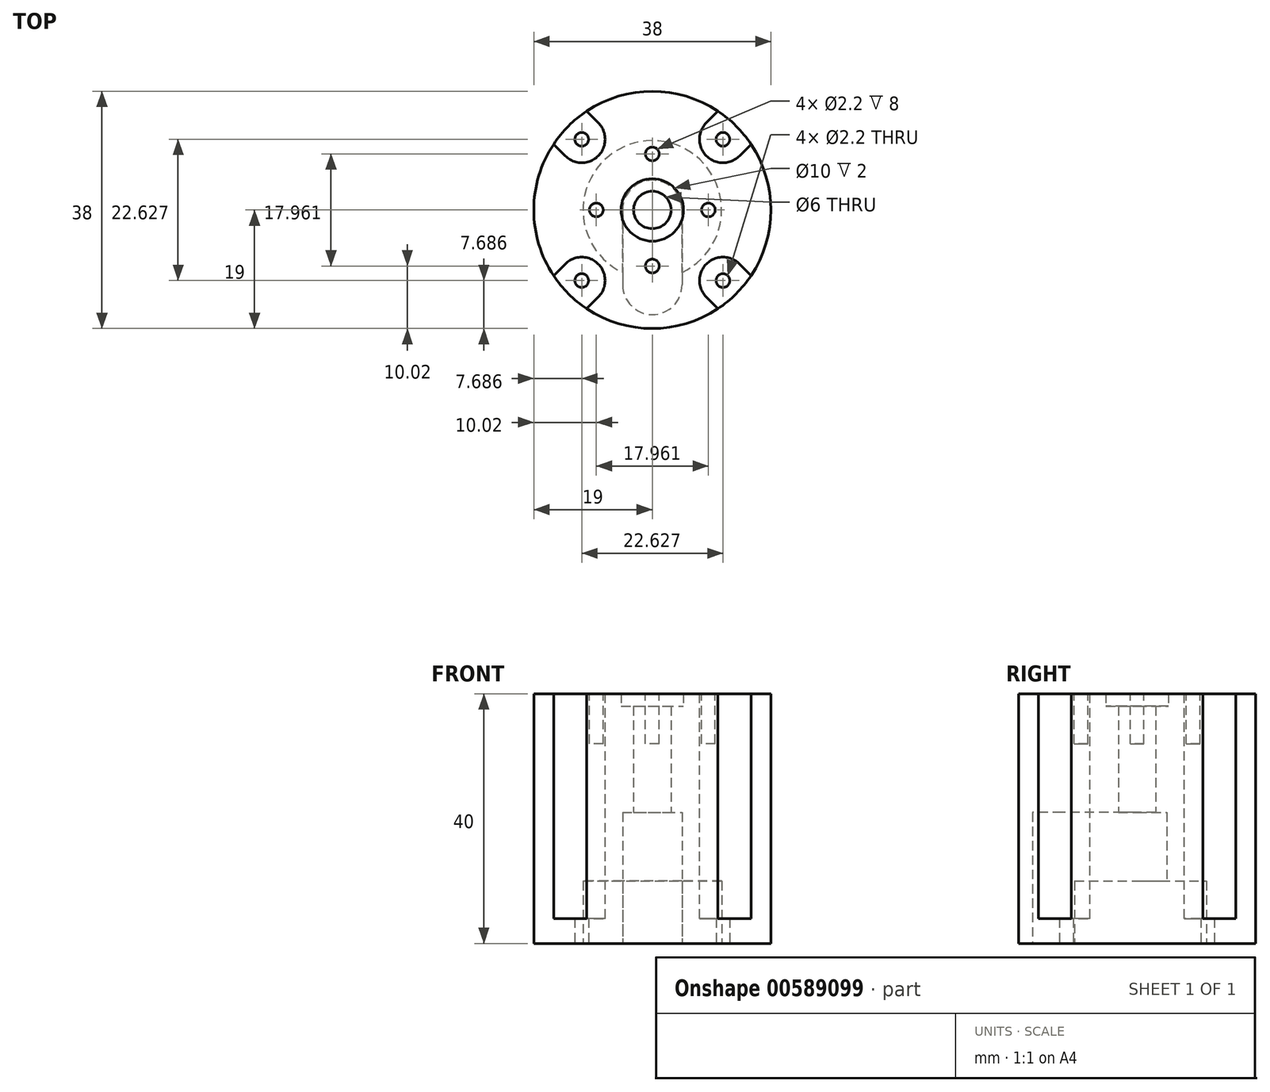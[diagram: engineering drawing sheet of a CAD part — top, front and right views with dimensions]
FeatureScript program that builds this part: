
annotation { "Feature Type Name" : "Feature", "Feature Type Description" : "" }
export const myFeature = defineFeature(function(context is Context, id is Id, definition is map)
    precondition{}
    {
        {
            var Q0;
            Q0=qCreatedBy(makeId("Front.planeOp"),FACE);
            var sketch = newSketch(context, id + "F0", { "sketchPlane" : qUnion([Q0])});
            skLineSegment(sketch, "E0", {"start": v(-11.1, 0) * mm, "end": v(-11.1, 10) * mm});
            skLineSegment(sketch, "E1", {"start": v(-11.1, 10) * mm, "end": v(0, 10) * mm});
            skLineSegment(sketch, "E2", {"start": v(-3, 21) * mm, "end": v(-3, 38) * mm});
            skLineSegment(sketch, "E3", {"start": v(-5, 40) * mm, "end": v(-19, 40) * mm});
            skLineSegment(sketch, "E4", {"start": v(-19, 40) * mm, "end": v(-19, 0) * mm});
            skLineSegment(sketch, "E5", {"start": v(-19, 0) * mm, "end": v(-11.1, 0) * mm});
            skLineSegment(sketch, "E6", {"start": v(-5, 40) * mm, "end": v(-5, 38) * mm});
            skLineSegment(sketch, "E7", {"start": v(-5, 38) * mm, "end": v(-3, 38) * mm});
            skLineSegment(sketch, "E8", {"start": v(0, 10) * mm, "end": v(0, 21) * mm});
            skLineSegment(sketch, "E9", {"start": v(-3, 21) * mm, "end": v(0, 21) * mm});
            skSolve(sketch);
        }
        {
            var Q0;
            Q0 = qSketchRegion(id + "F0", true);
            var Q1;
            Q1=sQuery(id+"F0.wireOp",EDGE,"E8");
            revolve(context, id + "F1", {"entities" : qUnion([Q0]), "axis" : qUnion([Q1]), "revolveType" : RevolveType.FULL});
        }
        {
            var Q0;
            Q0=makeQuery(id+"F1.opRevolve","SWEPT_FACE",FACE,{"disambiguationData":[OSD([sQuery(id+"F0.wireOp",EDGE,"E3")])]});
            var sketch = newSketch(context, id + "F2", { "sketchPlane" : qUnion([Q0])});
            skArc(sketch, "E10", {"start": v(8.66, 13.97) * mm, "mid": v(8.66, 8.66) * mm, "end": v(13.97, 8.66) * mm});
            skLineSegment(sketch, "E11", {"start": v(0, 0) * mm, "end": v(11.31, 11.31) * mm, "construction": true});
            skPoint(sketch, "E12.center", {"position": v(0, 0) * mm});
            skLineSegment(sketch, "E13", {"start": v(11.31, 11.31) * mm, "end": v(8.66, 13.97) * mm, "construction": true});
            skLineSegment(sketch, "E14", {"start": v(8.66, 13.97) * mm, "end": v(11.5, 16.8) * mm});
            skLineSegment(sketch, "E15", {"start": v(11.31, 11.31) * mm, "end": v(13.97, 8.66) * mm, "construction": true});
            skLineSegment(sketch, "E16", {"start": v(13.97, 8.66) * mm, "end": v(16.8, 11.5) * mm});
            skLineSegment(sketch, "E17", {"start": v(16.8, 11.5) * mm, "end": v(11.5, 16.8) * mm});
            skArc(sketch, "E18.1.0", {"start": v(-13.97, 8.66) * mm, "mid": v(-8.66, 8.66) * mm, "end": v(-8.66, 13.97) * mm});
            skLineSegment(sketch, "E18.1.1", {"start": v(-8.66, 13.97) * mm, "end": v(-11.5, 16.8) * mm});
            skLineSegment(sketch, "E18.1.2", {"start": v(-13.97, 8.66) * mm, "end": v(-16.8, 11.5) * mm});
            skLineSegment(sketch, "E18.1.3", {"start": v(-11.5, 16.8) * mm, "end": v(-16.8, 11.5) * mm});
            skLineSegment(sketch, "E18.1.4", {"start": v(-11.31, 11.31) * mm, "end": v(-13.97, 8.66) * mm, "construction": true});
            skLineSegment(sketch, "E18.1.5", {"start": v(-11.31, 11.31) * mm, "end": v(-8.66, 13.97) * mm, "construction": true});
            skArc(sketch, "E18.2.0", {"start": v(-8.66, -13.97) * mm, "mid": v(-8.66, -8.66) * mm, "end": v(-13.97, -8.66) * mm});
            skLineSegment(sketch, "E18.2.1", {"start": v(-13.97, -8.66) * mm, "end": v(-16.8, -11.5) * mm});
            skLineSegment(sketch, "E18.2.2", {"start": v(-8.66, -13.97) * mm, "end": v(-11.5, -16.8) * mm});
            skLineSegment(sketch, "E18.2.3", {"start": v(-16.8, -11.5) * mm, "end": v(-11.5, -16.8) * mm});
            skLineSegment(sketch, "E18.2.4", {"start": v(-11.31, -11.31) * mm, "end": v(-8.66, -13.97) * mm, "construction": true});
            skLineSegment(sketch, "E18.2.5", {"start": v(-11.31, -11.31) * mm, "end": v(-13.97, -8.66) * mm, "construction": true});
            skArc(sketch, "E18.3.0", {"start": v(13.97, -8.66) * mm, "mid": v(8.66, -8.66) * mm, "end": v(8.66, -13.97) * mm});
            skLineSegment(sketch, "E18.3.1", {"start": v(8.66, -13.97) * mm, "end": v(11.5, -16.8) * mm});
            skLineSegment(sketch, "E18.3.2", {"start": v(13.97, -8.66) * mm, "end": v(16.8, -11.5) * mm});
            skLineSegment(sketch, "E18.3.3", {"start": v(11.5, -16.8) * mm, "end": v(16.8, -11.5) * mm});
            skLineSegment(sketch, "E18.3.4", {"start": v(11.31, -11.31) * mm, "end": v(13.97, -8.66) * mm, "construction": true});
            skLineSegment(sketch, "E18.3.5", {"start": v(11.31, -11.31) * mm, "end": v(8.66, -13.97) * mm, "construction": true});
            skSolve(sketch);
        }
        {
            var Q0;
            Q0 = qSketchRegion(id + "F2", true);
            extrude(context, id + "F3", {"entities" : qUnion([Q0]), "operationType" : NewBodyOperationType.REMOVE, "oppositeDirection" : true, "depth" : 36 * mm, "offsetDistance" : 25 * mm});
        }
        {
            var Q0;
            Q0=makeQuery(id+"F1.opRevolve","SWEPT_FACE",FACE,{"disambiguationData":[OSD([sQuery(id+"F0.wireOp",EDGE,"E3")])]});
            var sketch = newSketch(context, id + "F4", { "sketchPlane" : qUnion([Q0])});
            skLineSegment(sketch, "E19", {"start": v(-8.98, 0) * mm, "end": v(0, 0) * mm, "construction": true});
            skLineSegment(sketch, "E20", {"start": v(0, 0) * mm, "end": v(8.98, 0) * mm, "construction": true});
            skLineSegment(sketch, "E21", {"start": v(0, -8.98) * mm, "end": v(0, 0) * mm, "construction": true});
            skLineSegment(sketch, "E22", {"start": v(0, 8.98) * mm, "end": v(0, 0) * mm, "construction": true});
            skCircle(sketch, "E23", {"center": v(0, 8.98) * mm, "radius": 1.1 * mm});
            skCircle(sketch, "E24", {"center": v(8.98, 0) * mm, "radius": 1.1 * mm});
            skCircle(sketch, "E25", {"center": v(0, -8.98) * mm, "radius": 1.1 * mm});
            skCircle(sketch, "E26", {"center": v(-8.98, 0) * mm, "radius": 1.1 * mm});
            skSolve(sketch);
        }
        {
            var Q0;
            Q0 = qSketchRegion(id + "F4", true);
            extrude(context, id + "F5", {"entities" : qUnion([Q0]), "operationType" : NewBodyOperationType.REMOVE, "oppositeDirection" : true, "depth" : 8 * mm, "offsetDistance" : 25 * mm});
        }
        {
            var Q0;
            Q0=makeQuery(id+"F1.opRevolve","SWEPT_FACE",FACE,{"disambiguationData":[OSD([sQuery(id+"F0.wireOp",EDGE,"E5")])]});
            var sketch = newSketch(context, id + "F6", { "sketchPlane" : qUnion([Q0])});
            skLineSegment(sketch, "E27", {"start": v(0, 0) * mm, "end": v(11.31, 11.31) * mm, "construction": true});
            skCircle(sketch, "E28", {"center": v(11.31, 11.31) * mm, "radius": 1.1 * mm});
            skCircle(sketch, "E29.1.0", {"center": v(-11.31, 11.31) * mm, "radius": 1.1 * mm});
            skCircle(sketch, "E29.2.0", {"center": v(-11.31, -11.31) * mm, "radius": 1.1 * mm});
            skCircle(sketch, "E29.3.0", {"center": v(11.31, -11.31) * mm, "radius": 1.1 * mm});
            skPoint(sketch, "E29.center", {"position": v(0, 0) * mm});
            skLineSegment(sketch, "E30.bottom", {"start": v(-4.76, 0) * mm, "end": v(4.76, 0) * mm, "construction": true});
            skLineSegment(sketch, "E30.top", {"start": v(-4.76, 12) * mm, "end": v(4.76, 12) * mm, "construction": true});
            skLineSegment(sketch, "E30.left", {"start": v(-4.76, 0) * mm, "end": v(-4.76, 12) * mm});
            skLineSegment(sketch, "E30.right", {"start": v(4.76, 0) * mm, "end": v(4.76, 12) * mm});
            skArc(sketch, "E31", {"start": v(-4.76, 12) * mm, "mid": v(0, 16.76) * mm, "end": v(4.76, 12) * mm});
            skArc(sketch, "E32", {"start": v(4.76, 0) * mm, "mid": v(0, -4.76) * mm, "end": v(-4.76, 0) * mm});
            skSolve(sketch);
        }
        {
            var Q0;
            Q0 = qSketchRegion(id + "F6", true);
            extrude(context, id + "F7", {"entities" : qUnion([Q0]), "operationType" : NewBodyOperationType.REMOVE, "oppositeDirection" : true, "depth" : 21 * mm, "offsetDistance" : 25 * mm});
        }
    });
